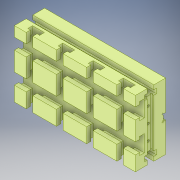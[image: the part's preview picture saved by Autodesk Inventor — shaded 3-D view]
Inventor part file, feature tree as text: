
AUTODESK INVENTOR PART (.ipt)
format: ipt  version: 2019 (Build 230136000, 136)  size: 413,184 bytes
history: native  units: mm
features: sketch x9, other x5, pattern_linear x5, mirror x3, hole x3, extrude x1
ambient origin geometry x8: Origin, YZ Plane, XZ Plane, XY Plane, X Axis, Y Axis, Z Axis, Center Point
bodies: Solid1 (feature_tree)
feature tree (26):
  extrude  "Extrusion1"  Depth=256.0mm
  other  "iFeature2:1"
  other  "iFeature2:2"
  pattern_linear  "Rectangular Pattern1"  Count1=7  [1 undecoded]
  pattern_linear  "Rectangular Pattern2"  Count1=4  [1 undecoded]
  other  "iFeature2:3"
  mirror  "Mirror1"
  other  "iFeature2:4"
  other  "iFeature2:5"
  mirror  "Mirror2"
  hole  "Hole1"  [1 undecoded]
  pattern_linear  "Rectangular Pattern3"  Spacing1=64.0mm  [1 undecoded]
  mirror  "Mirror3"
  hole  "Hole2"  [1 undecoded]
  pattern_linear  "Rectangular Pattern4"  Spacing1=32.0mm  [1 undecoded]
  hole  "Hole3"  [1 undecoded]
  pattern_linear  "Rectangular Pattern5"  Spacing1=38.0mm  [1 undecoded]
  sketch  "Sketch1"  dims[d0=140.0mm d1=256.0mm d2=70.0mm]
  sketch  "Sketch7"  dims[d15=10.0mm d16=25.0mm d17=10.0mm d18=9.0mm d19=14.0mm d20=9.0mm d21=12.5mm d22=7.0mm]
  sketch  "Sketch8"  dims[d23=38.0mm d24=40.0mm]
  sketch  "Sketch9"  dims[d26=64.0mm d27=20.0mm d29=64.0mm d30=20.0mm d32=10.0mm d33=10.0mm d34=25.0mm d35=10.0mm d36=9.0mm d37=14.0mm d38=9.0mm d39=12.5mm d40=7.0mm d41=32.0mm d42=7.0mm d43=2.0mm d44=2.0mm d45=5.0mm d46=135.0deg d47=7.0mm d48=7.0mm d49=2.0mm d50=2.0mm d51=5.0mm d52=135.0deg d53=7.0mm d54=32.0mm d55=4.917mm d56=10.0mm d57=4.0mm d58=2.0mm d59=90.0deg d60=15.0mm d61=20.594885mm d62=38.0mm d63=32.0mm d64=30.0mm d66=32.0mm d67=64.0mm d68=70.0mm d69=46.0mm d70=10.0mm d71=4.0mm d72=2.0mm d73=90.0deg d74=35.0mm d75=20.594885mm d76=30.0mm d78=64.0mm d79=10.0mm d81=64.0mm d82=32.0mm d83=70.0mm d84=4.917mm d85=10.0mm d86=4.0mm d87=2.0mm d88=90.0deg d89=15.0mm d90=20.594885mm d91=40.0mm d93=64.0mm]
  sketch  "Sketch2"  dims[d3=128.0mm]
  sketch  "Sketch3"  dims[d4=64.0mm]
  sketch  "Sketch4"  dims[d5=0.0mm]
  sketch  "Sketch5"  dims[d6=10.0mm d7=25.0mm d8=10.0mm d9=9.0mm d10=14.0mm d11=9.0mm d12=12.5mm d13=7.0mm]
  sketch  "Sketch6"  dims[d14=32.0mm]
note: 8 required parameter values undecoded (feature->parameter linkage not recoverable at this tier; creation-order binding heuristic only, values carry confidence <= 0.55)
